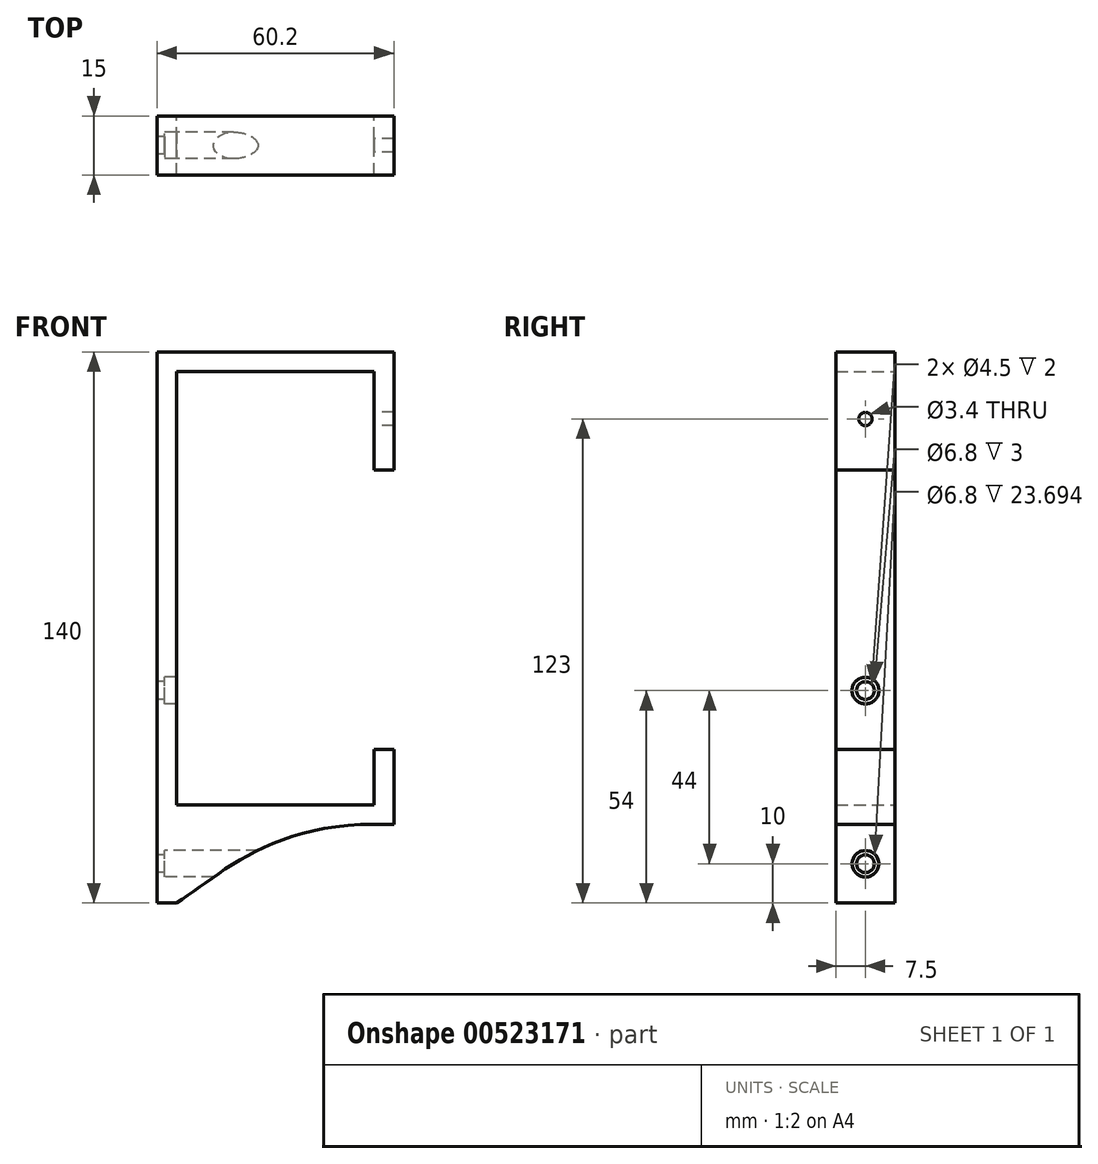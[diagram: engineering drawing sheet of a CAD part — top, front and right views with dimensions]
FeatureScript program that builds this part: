
annotation { "Feature Type Name" : "Feature", "Feature Type Description" : "" }
export const myFeature = defineFeature(function(context is Context, id is Id, definition is map)
    precondition{}
    {
        {
            var Q0;
            Q0=qCreatedBy(makeId("Right.planeOp"),FACE);
            var sketch = newSketch(context, id + "F0", { "sketchPlane" : qUnion([Q0])});
            skLineSegment(sketch, "E0.bottom", {"start": v(0, 0) * mm, "end": v(-15, 0) * mm});
            skLineSegment(sketch, "E0.top", {"start": v(0, 120) * mm, "end": v(-15, 120) * mm});
            skLineSegment(sketch, "E0.left", {"start": v(0, 0) * mm, "end": v(0, 120) * mm});
            skLineSegment(sketch, "E0.right", {"start": v(-15, 0) * mm, "end": v(-15, 120) * mm});
            skCircle(sketch, "E1", {"center": v(-7.5, -10) * mm, "radius": 2.25 * mm});
            skCircle(sketch, "E2", {"center": v(-7.5, -10) * mm, "radius": 3.4 * mm});
            skCircle(sketch, "E3", {"center": v(-7.5, 34) * mm, "radius": 3.4 * mm});
            skCircle(sketch, "E4", {"center": v(-7.5, 34) * mm, "radius": 2.25 * mm});
            skLineSegment(sketch, "E5.top", {"start": v(0, 117) * mm, "end": v(-15, 117) * mm});
            skLineSegment(sketch, "E5.left", {"start": v(0, 120) * mm, "end": v(0, 117) * mm});
            skLineSegment(sketch, "E5.right", {"start": v(-15, 120) * mm, "end": v(-15, 117) * mm});
            skLineSegment(sketch, "E6", {"start": v(-7.5, 117) * mm, "end": v(-7.5, 103) * mm});
            skCircle(sketch, "E7", {"center": v(-7.5, 103) * mm, "radius": 1.7 * mm});
            skLineSegment(sketch, "E8.top", {"start": v(0, -20) * mm, "end": v(-15, -20) * mm});
            skLineSegment(sketch, "E8.left", {"start": v(0, 0) * mm, "end": v(0, -20) * mm});
            skLineSegment(sketch, "E8.right", {"start": v(-15, 0) * mm, "end": v(-15, -20) * mm});
            skSolve(sketch);
        }
        {
            var Q0;
            Q0=qCreatedBy(makeId("Front.planeOp"),FACE);
            var sketch = newSketch(context, id + "F1", { "sketchPlane" : qUnion([Q0])});
            skLineSegment(sketch, "E9.bottom", {"start": v(0, 0) * mm, "end": v(5, 0) * mm});
            skLineSegment(sketch, "E9.top", {"start": v(0, 120) * mm, "end": v(5, 120) * mm});
            skLineSegment(sketch, "E9.left", {"start": v(0, 0) * mm, "end": v(0, 120) * mm});
            skLineSegment(sketch, "E9.right", {"start": v(5, 0) * mm, "end": v(5, 120) * mm});
            skLineSegment(sketch, "E10.bottom", {"start": v(5, 0) * mm, "end": v(55.2, 0) * mm});
            skLineSegment(sketch, "E10.top", {"start": v(5, 5) * mm, "end": v(55.2, 5) * mm});
            skLineSegment(sketch, "E10.left", {"start": v(5, 0) * mm, "end": v(5, 5) * mm});
            skLineSegment(sketch, "E10.right", {"start": v(55.2, 0) * mm, "end": v(55.2, 5) * mm});
            skLineSegment(sketch, "E11.top", {"start": v(0, -20) * mm, "end": v(5, -20) * mm});
            skLineSegment(sketch, "E11.left", {"start": v(0, 0) * mm, "end": v(0, -20) * mm});
            skLineSegment(sketch, "E11.right", {"start": v(5, 0) * mm, "end": v(5, -20) * mm});
            skFitSpline(sketch, "E12", {"points": [v(5, -20) * mm, v(55.2, 0) * mm], "startDerivative": vector(31.79, 20.7) * mm, "endDerivative": vector(79.85, 0) * mm});
            skLineSegment(sketch, "E13", {"start": v(0, -10) * mm, "end": v(5, -10) * mm});
            skLineSegment(sketch, "E14", {"start": v(0, 34) * mm, "end": v(5, 34) * mm});
            skLineSegment(sketch, "E15.bottom", {"start": v(55.2, 0) * mm, "end": v(60.2, 0) * mm});
            skLineSegment(sketch, "E15.top", {"start": v(55.2, 19) * mm, "end": v(60.2, 19) * mm});
            skLineSegment(sketch, "E15.left", {"start": v(55.2, 0) * mm, "end": v(55.2, 19) * mm});
            skLineSegment(sketch, "E15.right", {"start": v(60.2, 0) * mm, "end": v(60.2, 19) * mm});
            skLineSegment(sketch, "E16.bottom", {"start": v(5, 120) * mm, "end": v(55.2, 120) * mm});
            skLineSegment(sketch, "E16.top", {"start": v(5, 115) * mm, "end": v(55.2, 115) * mm});
            skLineSegment(sketch, "E16.left", {"start": v(5, 120) * mm, "end": v(5, 115) * mm});
            skLineSegment(sketch, "E16.right", {"start": v(55.2, 120) * mm, "end": v(55.2, 115) * mm});
            skLineSegment(sketch, "E17.bottom", {"start": v(55.2, 120) * mm, "end": v(60.2, 120) * mm});
            skLineSegment(sketch, "E17.top", {"start": v(55.2, 90) * mm, "end": v(60.2, 90) * mm});
            skLineSegment(sketch, "E17.left", {"start": v(55.2, 120) * mm, "end": v(55.2, 90) * mm});
            skLineSegment(sketch, "E17.right", {"start": v(60.2, 120) * mm, "end": v(60.2, 90) * mm});
            skLineSegment(sketch, "E18", {"start": v(55.2, 101) * mm, "end": v(60.2, 101) * mm});
            skSolve(sketch);
        }
        {
            var Q0;
            Q0 = qSketchRegion(id + "F1", true);
            extrude(context, id + "F2", {"entities" : qUnion([Q0]), "depth" : 15 * mm, "offsetDistance" : 25 * mm});
        }
        {
            var Q0;
            Q0=makeQuery(id+"F0.imprint","IMPRINT",FACE,{"disambiguationData":[TD([[makeQuery(id+"F0.imprint","IMPRINT",EDGE,{"derivedFrom":sQuery(id+"F0.wireOp",EDGE,"E7")}),1.0]])]});
            var Q1;
            Q1=sQuery(id+"F0.wireOp",EDGE,"E7");
            extrude(context, id + "F3", {"entities" : qUnion([Q0]), "operationType" : NewBodyOperationType.REMOVE, "surfaceEntities" : qUnion([Q1]), "depth" : 74 * mm, "offsetDistance" : 25 * mm, "hasSecondDirection" : true, "secondDirectionOppositeDirection" : false, "secondDirectionDepth" : 25 * mm});
        }
        {
            var Q0;
            Q0=makeQuery(id+"F0.imprint","IMPRINT",FACE,{"disambiguationData":[TD([[makeQuery(id+"F0.imprint","IMPRINT",EDGE,{"derivedFrom":sQuery(id+"F0.wireOp",EDGE,"E4")}),1.0]])]});
            var Q1;
            Q1=makeQuery(id+"F0.imprint","IMPRINT",FACE,{"disambiguationData":[TD([[makeQuery(id+"F0.imprint","IMPRINT",EDGE,{"derivedFrom":sQuery(id+"F0.wireOp",EDGE,"E1")}),1.0]])]});
            var Q2;
            Q2=sQuery(id+"F0.wireOp",EDGE,"E4");
            var Q3;
            Q3=sQuery(id+"F0.wireOp",EDGE,"E1");
            extrude(context, id + "F4", {"entities" : qUnion([Q0, Q1]), "operationType" : NewBodyOperationType.REMOVE, "surfaceEntities" : qUnion([Q2, Q3]), "depth" : 38.6 * mm, "offsetDistance" : 25 * mm});
        }
        {
            var Q0;
            Q0=makeQuery(id+"F0.imprint","IMPRINT",FACE,{"disambiguationData":[TD([[makeQuery(id+"F0.imprint","IMPRINT",EDGE,{"derivedFrom":sQuery(id+"F0.wireOp",EDGE,"E1")}),-1.0]])]});
            var Q1;
            Q1=makeQuery(id+"F0.imprint","IMPRINT",FACE,{"disambiguationData":[TD([[makeQuery(id+"F0.imprint","IMPRINT",EDGE,{"derivedFrom":sQuery(id+"F0.wireOp",EDGE,"E3")}),1.0]])]});
            var Q2;
            Q2=sQuery(id+"F0.wireOp",EDGE,"E2");
            var Q3;
            Q3=sQuery(id+"F0.wireOp",EDGE,"E3");
            extrude(context, id + "F5", {"entities" : qUnion([Q0, Q1]), "operationType" : NewBodyOperationType.REMOVE, "surfaceEntities" : qUnion([Q2, Q3]), "depth" : 49.7 * mm, "offsetDistance" : 25 * mm, "hasSecondDirection" : true, "secondDirectionOppositeDirection" : false, "secondDirectionDepth" : 2 * mm});
        }
    });
